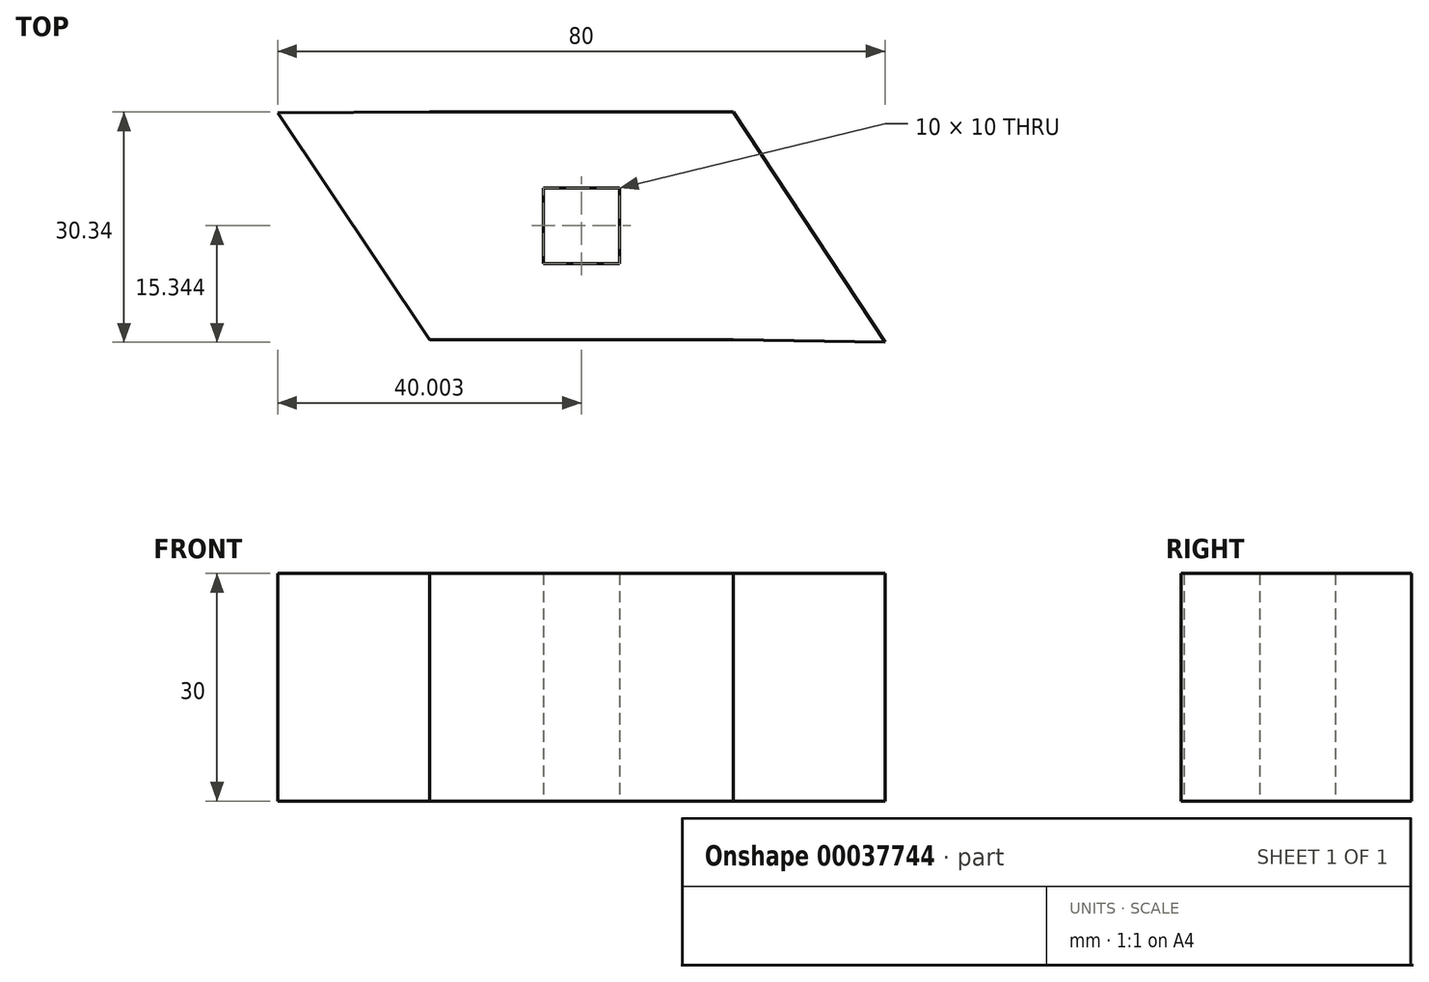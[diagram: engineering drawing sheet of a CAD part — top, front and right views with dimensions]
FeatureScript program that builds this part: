
annotation { "Feature Type Name" : "Feature", "Feature Type Description" : "" }
export const myFeature = defineFeature(function(context is Context, id is Id, definition is map)
    precondition{}
    {
        {
            var Q0;
            Q0=qCreatedBy(makeId("Top.planeOp"),FACE);
            var sketch = newSketch(context, id + "F0", { "sketchPlane" : qUnion([Q0])});
            skLineSegment(sketch, "E0.bottom", {"start": v(-47.55, 10.28) * mm, "end": v(-7.55, 10.28) * mm});
            skLineSegment(sketch, "E0.top", {"start": v(-47.55, -19.72) * mm, "end": v(-7.55, -19.72) * mm});
            skLineSegment(sketch, "E0.left", {"start": v(-47.55, 10.28) * mm, "end": v(-47.55, -19.72) * mm});
            skLineSegment(sketch, "E0.right", {"start": v(-7.55, 10.28) * mm, "end": v(-7.55, -19.72) * mm});
            skLineSegment(sketch, "E1", {"start": v(-7.55, 10.28) * mm, "end": v(12.45, -20.06) * mm});
            skLineSegment(sketch, "E2", {"start": v(12.45, -20.06) * mm, "end": v(-7.55, -19.72) * mm});
            skLineSegment(sketch, "E3", {"start": v(-47.55, -19.72) * mm, "end": v(-67.55, 10.18) * mm});
            skLineSegment(sketch, "E4", {"start": v(-67.55, 10.18) * mm, "end": v(-47.55, 10.28) * mm});
            skLineSegment(sketch, "E5.bottom", {"start": v(-32.55, 0.28) * mm, "end": v(-22.55, 0.28) * mm});
            skLineSegment(sketch, "E5.top", {"start": v(-32.55, -9.72) * mm, "end": v(-22.55, -9.72) * mm});
            skLineSegment(sketch, "E5.left", {"start": v(-32.55, 0.28) * mm, "end": v(-32.55, -9.72) * mm});
            skLineSegment(sketch, "E5.right", {"start": v(-22.55, 0.28) * mm, "end": v(-22.55, -9.72) * mm});
            skLineSegment(sketch, "E6", {"start": v(-24.58, 10.28) * mm, "end": v(-24.58, 0.28) * mm, "construction": true});
            skLineSegment(sketch, "E7", {"start": v(-27.55, -9.72) * mm, "end": v(-27.55, -19.72) * mm, "construction": true});
            skPoint(sketch, "E7.endSnap0", {"position": v(-27.55, -19.72) * mm});
            skLineSegment(sketch, "E8", {"start": v(-47.55, -4.72) * mm, "end": v(-32.55, -4.72) * mm, "construction": true});
            skLineSegment(sketch, "E9", {"start": v(-22.55, -4.72) * mm, "end": v(-7.55, -4.72) * mm, "construction": true});
            skSolve(sketch);
        }
        {
            var Q0;
            Q0=makeQuery(id+"F0.imprint","IMPRINT",FACE,{"disambiguationData":[TD([[makeQuery(id+"F0.imprint","IMPRINT",EDGE,{"derivedFrom":sQuery(id+"F0.wireOp",EDGE,"E0.left")}),-1.0]])]});
            var Q1;
            Q1=makeQuery(id+"F0.imprint","IMPRINT",FACE,{"disambiguationData":[TD([[makeQuery(id+"F0.imprint","IMPRINT",EDGE,{"derivedFrom":sQuery(id+"F0.wireOp",EDGE,"E0.bottom")}),-1.0]])]});
            var Q2;
            Q2=makeQuery(id+"F0.imprint","IMPRINT",FACE,{"disambiguationData":[TD([[makeQuery(id+"F0.imprint","IMPRINT",EDGE,{"derivedFrom":sQuery(id+"F0.wireOp",EDGE,"E0.right")}),1.0]])]});
            extrude(context, id + "F1", {"entities" : qUnion([Q0, Q1, Q2]), "depth" : 30 * mm});
        }
    });
